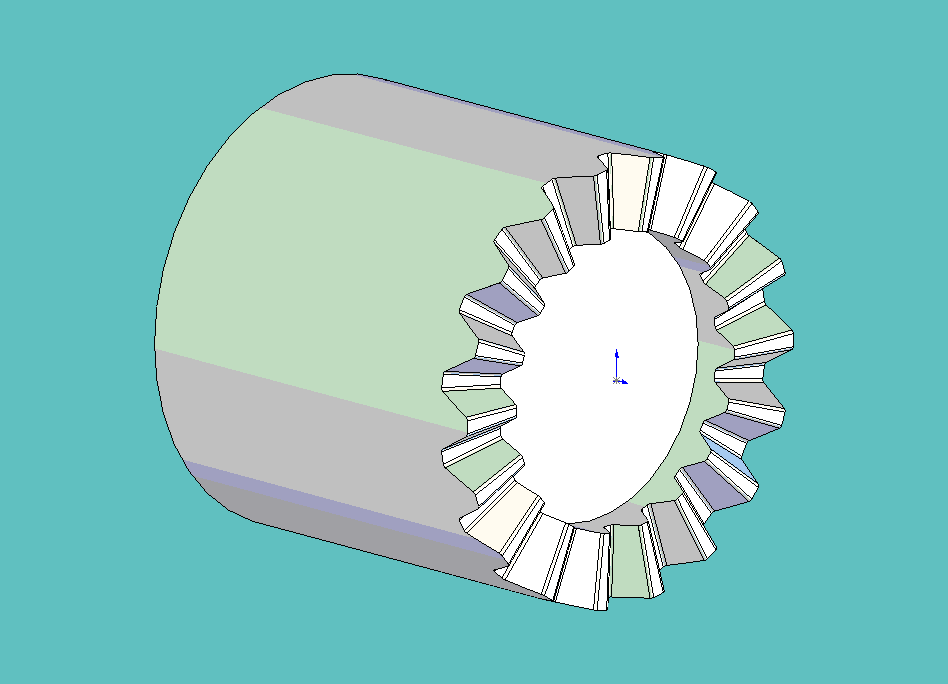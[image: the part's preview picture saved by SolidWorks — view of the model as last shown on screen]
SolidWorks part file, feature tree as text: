
SOLIDWORKS PART (.sldprt)
format: sldprt  version: not decoded by parser v0  size: 640,512 bytes
history: native  units: mm
features: sketch x5, plane x4, extrude x2, material x1, cut_revolve x1, fillet x1, pattern_circular x1 (+8 scaffold rows collapsed)
feature tree (23):
  scaffold x8  (default folders/planes/origin — collapsed)
  material  "Material <nicht festgelegt>"
  plane  "Vorne"
  plane  "Oben"
  plane  "Rechts"
  sketch  "Layout"  dims[c1.D2=60.0mm c1.D3=~44.152131mm c1.D1=~79.067015mm c2.D1=10.0deg c2.D3=10.0mm]
  plane  "Ebene tangential"
  sketch  "Profil (Aussen)"  dims[c1.D1=5.0mm c1.D2=~10.607794mm c2.D2=60.0deg c2.D3=2.5mm]
  sketch  "Punkt (Mitte)"
  extrude  "Ring"  Depth=5mm
  sketch  "Skizze3"
  extrude  "Welle D60x50"  Depth=50mm
  sketch  "Skizze5"
  cut_revolve  "Konus Endfläche"  Angle=360deg
  fillet  "Verrundung Nut"  Radius=0.5mm
  pattern_circular  "Kreismuster Nut"  Count=18 Angle=360deg
decode coverage: 7 of 10 modeling features carry decoded parameters
note: ~ marks probable driven/reference dimensions
note: suppression state not decoded; provenance and decode notes live in map.json
